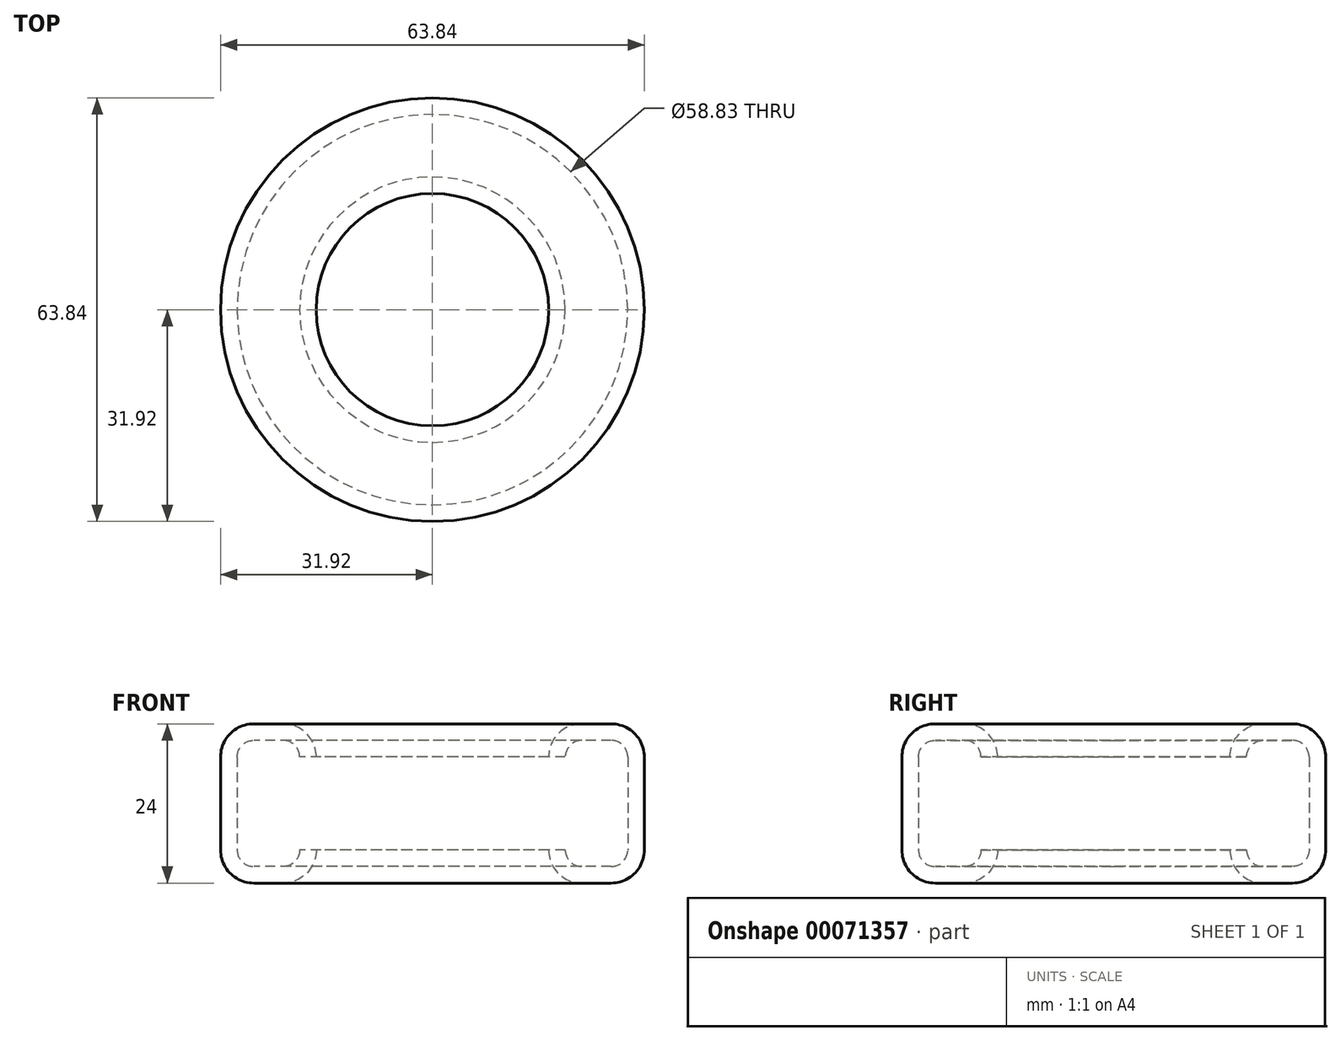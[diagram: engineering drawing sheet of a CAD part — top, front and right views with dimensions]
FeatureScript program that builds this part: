
annotation { "Feature Type Name" : "Feature", "Feature Type Description" : "" }
export const myFeature = defineFeature(function(context is Context, id is Id, definition is map)
    precondition{}
    {
        {
            var Q0;
            Q0=qCreatedBy(makeId("Top.planeOp"),FACE);
            var sketch = newSketch(context, id + "F0", { "sketchPlane" : qUnion([Q0])});
            skCircle(sketch, "E0", {"center": v(0, 0) * mm, "radius": 17.5 * mm});
            skCircle(sketch, "E1", {"center": v(0, 0) * mm, "radius": 31.91 * mm});
            skSolve(sketch);
        }
        {
            var Q0;
            Q0=makeQuery(id+"F0.imprint","IMPRINT",FACE,{"disambiguationData":[TD([[makeQuery(id+"F0.imprint","IMPRINT",EDGE,{"derivedFrom":sQuery(id+"F0.wireOp",EDGE,"E0")}),-1.0]])]});
            extrude(context, id + "F1", {"entities" : qUnion([Q0]), "depth" : 24 * mm});
        }
        {
            var Q0;
            Q0=makeQuery(id+"F1.opExtrude","CAP_EDGE",EDGE,{"disambiguationData":[OSD([sQuery(id+"F0.wireOp",EDGE,"E1")])],"isStart":false});
            var Q1;
            Q1=makeQuery(id+"F1.opExtrude","CAP_EDGE",EDGE,{"disambiguationData":[OSD([sQuery(id+"F0.wireOp",EDGE,"E0")])],"isStart":false});
            var Q2;
            Q2=makeQuery(id+"F1.opExtrude","CAP_EDGE",EDGE,{"disambiguationData":[OSD([sQuery(id+"F0.wireOp",EDGE,"E1")])],"isStart":true});
            var Q3;
            Q3=makeQuery(id+"F1.opExtrude","CAP_EDGE",EDGE,{"disambiguationData":[OSD([sQuery(id+"F0.wireOp",EDGE,"E0")])],"isStart":true});
            fillet(context, id + "F2", {"entities" : qUnion([Q0, Q1, Q2, Q3]), "radius" : 5 * mm, "tangentPropagation" : true, "allowEdgeOverflow" : false});
        }
        {
            var Q0;
            Q0=makeQuery(id+"F1.opExtrude","SWEPT_FACE",FACE,{"disambiguationData":[OSD([sQuery(id+"F0.wireOp",EDGE,"E0")])]});
            shell(context, id + "F3", {"entities" : qUnion([Q0]), "thickness" : 2.5 * mm});
        }
    });
